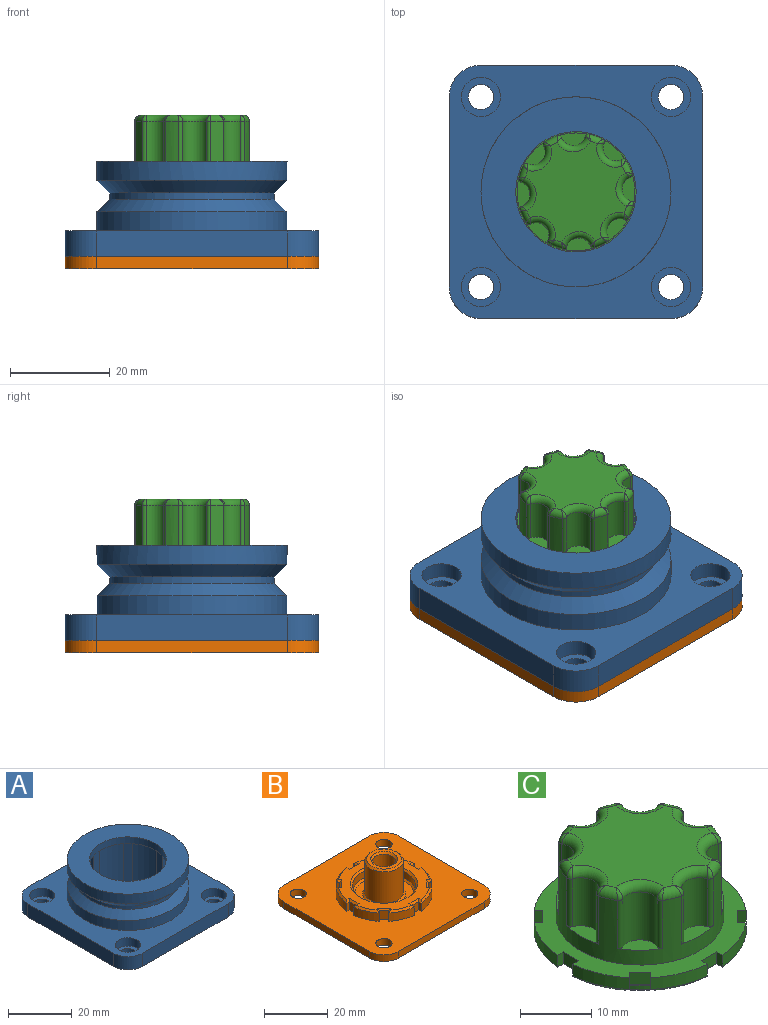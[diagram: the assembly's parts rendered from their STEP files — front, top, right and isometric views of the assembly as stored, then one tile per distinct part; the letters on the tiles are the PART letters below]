
ASSEMBLY  parts=3 mates=5
PART A: 62 faces, bbox 50.8x50.8x19.1 mm
  f0: cylinder r=19.05mm len=38.1mm, axis (0,0,-1), area 456mm2, adj f15,f61
  f1: cylinder r=3.94mm len=7.87mm, axis (0,0,-1), area 78.5mm2, adj f26,f58
  f2: cylinder r=3.94mm len=7.87mm, axis (0,0,-1), area 78.5mm2, adj f26,f56
  f3: cylinder r=3.94mm len=7.87mm, axis (0,0,-1), area 78.5mm2, adj f26,f54
  f4: cylinder r=3.94mm len=7.87mm, axis (0,0,-1), area 78.5mm2, adj f26,f52
  f5: cylinder r=15.24mm len=16.51mm, axis (0,0,-1), area 155.6mm2, adj f12,f16,f46,f50
  f6: cylinder r=15.24mm len=16.51mm, axis (0,0,-1), area 155.6mm2, adj f12,f16,f28,f47
  f7: cylinder r=15.24mm len=16.51mm, axis (0,0,-1), area 155.6mm2, adj f12,f16,f40,f44
  f8: cylinder r=15.24mm len=16.51mm, axis (0,0,-1), area 155.6mm2, adj f12,f16,f37,f41
  f9: cylinder r=15.24mm len=16.51mm, axis (0,0,-1), area 155.6mm2, adj f12,f16,f34,f38
  f10: cylinder r=15.24mm len=16.51mm, axis (0,0,-1), area 155.6mm2, adj f12,f16,f31,f35
  f11: cylinder r=15.24mm len=16.51mm, axis (0,0,-1), area 155.6mm2, adj f12,f16,f32,f49
  f12: plane 30.37x30.37mm, normal (0,0,-1), area 246.9mm2, adj f5,f6,f7,f8,f9,f10,f11,f13
  f13: cylinder r=15.24mm len=16.51mm, axis (0,0,-1), area 155.6mm2, adj f12,f16,f29,f43
  f14: cylinder r=19.05mm len=38.1mm, axis (0,0,-1), area 456mm2, adj f26,f59
  f15: plane 38.1x38.1mm, normal (0,0,1), area 682.8mm2, adj f0,f17
  f16: plane 50.8x50.8mm, normal (0,0,-1), area 1760.7mm2, adj f5,f6,f7,f8,f9,f10,f11,f13
  f17: cylinder r=12.06mm len=24.13mm, axis (0,0,1), area 192.5mm2, adj f12,f15
  f18: cylinder r=6.35mm len=6.35mm, axis (0,0,-1), area 50.7mm2, adj f16,f19,f25,f26
  f19: plane 38.1x5.08mm, normal (0,-1,0), area 193.5mm2, adj f16,f18,f20,f26
  f20: cylinder r=6.35mm len=6.35mm, axis (0,0,-1), area 50.7mm2, adj f16,f19,f21,f26
  f21: plane 38.1x5.08mm, normal (-1,0,0), area 193.5mm2, adj f16,f20,f22,f26
  f22: cylinder r=6.35mm len=6.35mm, axis (0,0,-1), area 50.7mm2, adj f16,f21,f23,f26
  f23: plane 38.1x5.08mm, normal (0,1,0), area 193.5mm2, adj f16,f22,f24,f26
  f24: cylinder r=6.35mm len=6.35mm, axis (0,0,-1), area 50.7mm2, adj f16,f23,f25,f26
  f25: plane 38.1x5.08mm, normal (1,0,0), area 193.5mm2, adj f16,f18,f24,f26
  f26: plane 50.8x50.8mm, normal (0,0,1), area 1211.2mm2, adj f1,f2,f3,f4,f14,f18,f19,f20
  f27: plane 16.51x2.54mm, normal (0,1,0), area 41.9mm2, adj f12,f16,f28,f29
  f28: plane 16.51x1.22mm, normal (1,0,0), area 20.1mm2, adj f6,f12,f16,f27
  f29: plane 16.51x1.22mm, normal (-1,0,0), area 20.1mm2, adj f12,f13,f16,f27
  f30: plane 16.51x1.8mm, normal (-0.71,-0.71,0), area 41.9mm2, adj f12,f16,f31,f32
  f31: plane 16.51x0.86mm, normal (-0.71,0.71,0), area 20.1mm2, adj f10,f12,f16,f30
  f32: plane 16.51x0.86mm, normal (0.71,-0.71,0), area 20.1mm2, adj f11,f12,f16,f30
  f33: plane 16.51x2.54mm, normal (0,-1,0), area 41.9mm2, adj f12,f16,f34,f35
  f34: plane 16.51x1.22mm, normal (-1,0,0), area 20.1mm2, adj f9,f12,f16,f33
  f35: plane 16.51x1.22mm, normal (1,0,0), area 20.1mm2, adj f10,f12,f16,f33
  f36: plane 16.51x1.8mm, normal (0.71,-0.71,0), area 41.9mm2, adj f12,f16,f37,f38
  f37: plane 16.51x0.86mm, normal (-0.71,-0.71,0), area 20.1mm2, adj f8,f12,f16,f36
  f38: plane 16.51x0.86mm, normal (0.71,0.71,0), area 20.1mm2, adj f9,f12,f16,f36
  f39: plane 16.51x2.54mm, normal (1,0,0), area 41.9mm2, adj f12,f16,f40,f41
  f40: plane 16.51x1.22mm, normal (0,-1,0), area 20.1mm2, adj f7,f12,f16,f39
  f41: plane 16.51x1.22mm, normal (0,1,0), area 20.1mm2, adj f8,f12,f16,f39
  f42: plane 16.51x1.8mm, normal (0.71,0.71,0), area 41.9mm2, adj f12,f16,f43,f44
  f43: plane 16.51x0.86mm, normal (0.71,-0.71,0), area 20.1mm2, adj f12,f13,f16,f42
  f44: plane 16.51x0.86mm, normal (-0.71,0.71,0), area 20.1mm2, adj f7,f12,f16,f42
  f45: plane 16.51x1.8mm, normal (-0.71,0.71,0), area 41.9mm2, adj f12,f16,f46,f47
  f46: plane 16.51x0.86mm, normal (0.71,0.71,0), area 20.1mm2, adj f5,f12,f16,f45
  f47: plane 16.51x0.86mm, normal (-0.71,-0.71,0), area 20.1mm2, adj f6,f12,f16,f45
  f48: plane 16.51x2.54mm, normal (-1,0,0), area 41.9mm2, adj f12,f16,f49,f50
  f49: plane 16.51x1.22mm, normal (0,1,0), area 20.1mm2, adj f11,f12,f16,f48
  f50: plane 16.51x1.22mm, normal (0,-1,0), area 20.1mm2, adj f5,f12,f16,f48
  f51: cylinder r=2.54mm len=5.08mm, axis (0,0,-1), area 30.4mm2, adj f16,f52
  f52: plane 7.87x7.87mm, normal (0,0,1), area 28.4mm2, adj f4,f51
  f53: cylinder r=2.54mm len=5.08mm, axis (0,0,-1), area 30.4mm2, adj f16,f54
  f54: plane 7.87x7.87mm, normal (0,0,1), area 28.4mm2, adj f3,f53
  f55: cylinder r=2.54mm len=5.08mm, axis (0,0,-1), area 30.4mm2, adj f16,f56
  f56: plane 7.87x7.87mm, normal (0,0,1), area 28.4mm2, adj f2,f55
  f57: cylinder r=2.54mm len=5.08mm, axis (0,0,-1), area 30.4mm2, adj f16,f58
  f58: plane 7.87x7.87mm, normal (0,0,1), area 28.4mm2, adj f1,f57
  f59: cone r=16.51mm half-angle=45deg, axis (0,0,-1), area 401.3mm2, adj f14,f60
  f60: cylinder r=16.51mm len=33.02mm, axis (0,0,-1), area 131.7mm2, adj f59,f61
  f61: cone r=16.51mm half-angle=45deg, axis (0,0,1), area 401.3mm2, adj f0,f60
PART B: 90 faces, bbox 50.8x50.8x15.9 mm
  f0: plane 50.8x50.8mm, normal (0,0,1), area 1777.7mm2, adj f1,f2,f3,f4,f5,f6,f7,f8
  f1: cylinder r=6.35mm len=6.35mm, axis (0,0,-1), area 25.3mm2, adj f0,f2,f11,f13
  f2: plane 38.1x2.54mm, normal (0,1,0), area 96.8mm2, adj f0,f1,f3,f13
  f3: cylinder r=6.35mm len=6.35mm, axis (0,0,-1), area 25.3mm2, adj f0,f2,f4,f13
  f4: plane 38.1x2.54mm, normal (-1,0,0), area 96.8mm2, adj f0,f3,f5,f13
  f5: cylinder r=6.35mm len=6.35mm, axis (0,0,-1), area 25.3mm2, adj f0,f4,f6,f13
  f6: plane 38.1x2.54mm, normal (0,-1,0), area 96.8mm2, adj f0,f5,f7,f13
  f7: cylinder r=6.35mm len=6.35mm, axis (0,0,-1), area 25.3mm2, adj f0,f6,f11,f13
  f8: cylinder r=2.54mm len=5.08mm, axis (0,0,-1), area 40.5mm2, adj f0,f13
  f9: cylinder r=2.54mm len=5.08mm, axis (0,0,-1), area 40.5mm2, adj f0,f13
  f10: cylinder r=2.54mm len=5.08mm, axis (0,0,-1), area 40.5mm2, adj f0,f13
  f11: plane 38.1x2.54mm, normal (1,0,0), area 96.8mm2, adj f0,f1,f7,f13
  f12: cylinder r=2.54mm len=5.08mm, axis (0,0,-1), area 40.5mm2, adj f0,f13
  f13: plane 50.8x50.8mm, normal (0,0,-1), area 2465mm2, adj f1,f2,f3,f4,f5,f6,f7,f8
  f14: plane 3.18x1.19mm, normal (-1,0,0), area 3.8mm2, adj f0,f15,f45,f84
  f15: plane 3.18x3.05mm, normal (0,1,0), area 9.7mm2, adj f0,f14,f16,f82
  f16: plane 3.18x1.19mm, normal (1,0,0), area 3.8mm2, adj f0,f15,f17,f80
  f17: cylinder r=15.11mm len=8.03mm, axis (0,0,-1), area 28mm2, adj f0,f16,f18,f78
  f18: plane 3.18x0.84mm, normal (-0.71,-0.71,0), area 3.8mm2, adj f0,f17,f19,f76
  f19: plane 3.18x2.16mm, normal (-0.71,0.71,0), area 9.7mm2, adj f0,f18,f20,f74
  f20: plane 3.18x0.84mm, normal (0.71,0.71,0), area 3.8mm2, adj f0,f19,f21,f72
  f21: cylinder r=15.11mm len=8.03mm, axis (0,0,-1), area 28mm2, adj f0,f20,f22,f70
  f22: plane 3.18x1.19mm, normal (0,-1,0), area 3.8mm2, adj f0,f21,f23,f68
  f23: plane 3.18x3.05mm, normal (-1,0,0), area 9.7mm2, adj f0,f22,f24,f66
  f24: plane 3.18x1.19mm, normal (0,1,0), area 3.8mm2, adj f0,f23,f25,f64
  f25: cylinder r=15.11mm len=8.03mm, axis (0,0,-1), area 28mm2, adj f0,f24,f26,f62
  f26: plane 3.18x0.84mm, normal (0.71,-0.71,0), area 3.8mm2, adj f0,f25,f27,f60
  f27: plane 3.18x2.16mm, normal (-0.71,-0.71,0), area 9.7mm2, adj f0,f26,f28,f58
  f28: plane 3.18x0.84mm, normal (-0.71,0.71,0), area 3.8mm2, adj f0,f27,f29,f59
  f29: cylinder r=15.11mm len=8.03mm, axis (0,0,-1), area 28mm2, adj f0,f28,f30,f61
  f30: plane 3.18x1.19mm, normal (1,0,0), area 3.8mm2, adj f0,f29,f31,f63
  f31: plane 3.18x3.05mm, normal (0,-1,0), area 9.7mm2, adj f0,f30,f32,f65
  f32: plane 3.18x1.19mm, normal (-1,0,0), area 3.8mm2, adj f0,f31,f33,f67
  f33: cylinder r=15.11mm len=8.03mm, axis (0,0,-1), area 28mm2, adj f0,f32,f34,f69
  f34: plane 3.18x0.84mm, normal (0.71,0.71,0), area 3.8mm2, adj f0,f33,f35,f71
  f35: plane 3.18x2.16mm, normal (0.71,-0.71,0), area 9.7mm2, adj f0,f34,f36,f73
  f36: plane 3.18x0.84mm, normal (-0.71,-0.71,0), area 3.8mm2, adj f0,f35,f37,f75
  f37: cylinder r=15.11mm len=8.03mm, axis (0,0,-1), area 28mm2, adj f0,f36,f38,f77
  f38: plane 3.18x1.19mm, normal (0,1,0), area 3.8mm2, adj f0,f37,f39,f79
  f39: plane 3.18x3.05mm, normal (1,0,0), area 9.7mm2, adj f0,f38,f40,f81
  f40: plane 3.18x1.19mm, normal (0,-1,0), area 3.8mm2, adj f0,f39,f41,f83
  f41: cylinder r=15.11mm len=8.03mm, axis (0,0,-1), area 28mm2, adj f0,f40,f42,f85
  f42: plane 3.18x0.84mm, normal (-0.71,0.71,0), area 3.8mm2, adj f0,f41,f43,f87
  f43: plane 3.18x2.16mm, normal (0.71,0.71,0), area 9.7mm2, adj f0,f42,f44,f89
  f44: plane 3.18x0.84mm, normal (0.71,-0.71,0), area 3.8mm2, adj f0,f43,f45,f88
  f45: cylinder r=15.11mm len=8.03mm, axis (0,0,-1), area 28mm2, adj f0,f14,f44,f86
  f46: cylinder r=9.91mm len=19.81mm, axis (0,0,-1), area 158.1mm2, adj f54,f57
  f47: plane 28.63x28.63mm, normal (0,0,1), area 267.4mm2, adj f57,f58,f59,f60,f61,f62,f63,f64
  f48: plane 18.54x18.54mm, normal (0,0,1), area 127.7mm2, adj f53,f54
  f49: cylinder r=3.56mm len=7.11mm, axis (0,0,-1), area 156.1mm2, adj f52,f55
  f50: cylinder r=6.1mm len=12.19mm, axis (0,0,-1), area 462.1mm2, adj f53,f56
  f51: plane 10.92x10.92mm, normal (0,0,1), area 38.5mm2, adj f55,f56
  f52: plane 7.11x7.11mm, normal (0,0,1), area 39.7mm2, adj f49
  f53: cone r=6.1mm half-angle=45deg, axis (0,0,-1), area 36.2mm2, adj f48,f50
  f54: cone r=9.91mm half-angle=45deg, axis (0,0,1), area 54.1mm2, adj f46,f48
  f55: cone r=3.56mm half-angle=45deg, axis (0,0,1), area 21.9mm2, adj f49,f51
  f56: cone r=5.46mm half-angle=45deg, axis (0,0,-1), area 32.6mm2, adj f50,f51
  f57: cone r=9.91mm half-angle=45deg, axis (0,0,1), area 57.7mm2, adj f46,f47
  f58: plane 3.05x3.05mm, normal (-0.5,-0.5,0.71), area 3.3mm2, adj f27,f47,f59,f60
  f59: plane 1.76x0.86mm, normal (-0.5,0.5,0.71), area 1mm2, adj f28,f47,f58,f61
  f60: plane 1.76x0.86mm, normal (0.5,-0.5,0.71), area 1mm2, adj f26,f47,f58,f62
  f61: cone r=14.48mm half-angle=45deg, axis (0,0,-1), area 7.1mm2, adj f29,f47,f59,f63
  f62: cone r=14.48mm half-angle=45deg, axis (0,0,-1), area 7.1mm2, adj f25,f47,f60,f64
  f63: plane 1.84x0.65mm, normal (0.71,0,0.71), area 1mm2, adj f30,f47,f61,f65
  f64: plane 1.84x0.65mm, normal (0,0.71,0.71), area 1mm2, adj f24,f47,f62,f66
  f65: plane 4.32x0.64mm, normal (0,-0.71,0.71), area 3.3mm2, adj f31,f47,f63,f67
  f66: plane 4.32x0.64mm, normal (-0.71,0,0.71), area 3.3mm2, adj f23,f47,f64,f68
  f67: plane 1.84x0.65mm, normal (-0.71,0,0.71), area 1mm2, adj f32,f47,f65,f69
  f68: plane 1.84x0.65mm, normal (0,-0.71,0.71), area 1mm2, adj f22,f47,f66,f70
  f69: cone r=14.48mm half-angle=45deg, axis (0,0,-1), area 7.1mm2, adj f33,f47,f67,f71
  f70: cone r=14.48mm half-angle=45deg, axis (0,0,-1), area 7.1mm2, adj f21,f47,f68,f72
  f71: plane 1.76x0.86mm, normal (0.5,0.5,0.71), area 1mm2, adj f34,f47,f69,f73
  f72: plane 1.76x0.86mm, normal (0.5,0.5,0.71), area 1mm2, adj f20,f47,f70,f74
  f73: plane 3.05x3.05mm, normal (0.5,-0.5,0.71), area 3.3mm2, adj f35,f47,f71,f75
  f74: plane 3.05x3.05mm, normal (-0.5,0.5,0.71), area 3.3mm2, adj f19,f47,f72,f76
  f75: plane 1.76x0.86mm, normal (-0.5,-0.5,0.71), area 1mm2, adj f36,f47,f73,f77
  f76: plane 1.76x0.86mm, normal (-0.5,-0.5,0.71), area 1mm2, adj f18,f47,f74,f78
  f77: cone r=14.48mm half-angle=45deg, axis (0,0,-1), area 7.1mm2, adj f37,f47,f75,f79
  f78: cone r=14.48mm half-angle=45deg, axis (0,0,-1), area 7.1mm2, adj f17,f47,f76,f80
  f79: plane 1.84x0.65mm, normal (0,0.71,0.71), area 1mm2, adj f38,f47,f77,f81
  f80: plane 1.84x0.65mm, normal (0.71,0,0.71), area 1mm2, adj f16,f47,f78,f82
  f81: plane 4.32x0.64mm, normal (0.71,0,0.71), area 3.3mm2, adj f39,f47,f79,f83
  f82: plane 4.32x0.64mm, normal (0,0.71,0.71), area 3.3mm2, adj f15,f47,f80,f84
  f83: plane 1.84x0.65mm, normal (0,-0.71,0.71), area 1mm2, adj f40,f47,f81,f85
  f84: plane 1.84x0.65mm, normal (-0.71,0,0.71), area 1mm2, adj f14,f47,f82,f86
  f85: cone r=14.48mm half-angle=45deg, axis (0,0,-1), area 7.1mm2, adj f41,f47,f83,f87
  f86: cone r=14.48mm half-angle=45deg, axis (0,0,-1), area 7.1mm2, adj f45,f47,f84,f88
  f87: plane 1.76x0.86mm, normal (-0.5,0.5,0.71), area 1mm2, adj f42,f47,f85,f89
  f88: plane 1.76x0.86mm, normal (0.5,-0.5,0.71), area 1mm2, adj f44,f47,f86,f89
  f89: plane 3.05x3.05mm, normal (0.5,0.5,0.71), area 3.3mm2, adj f43,f47,f87,f88
PART C: 142 faces, bbox 29.8x29.8x18.4 mm
  f0: cylinder r=6.35mm len=12.7mm, axis (0,0,-1), area 491.5mm2, adj f106,f107
  f1: cylinder r=11.81mm len=23.62mm, axis (0,0,-1), area 377.4mm2, adj f11,f37,f38,f40,f41,f42,f44,f45
  f2: plane 19.99x19.99mm, normal (0,0,1), area 253.4mm2, adj f74,f77,f78,f81,f82,f85,f86,f89
  f3: cylinder r=14.99mm len=7.94mm, axis (0,0,-1), area 17.7mm2, adj f11,f24,f35,f125
  f4: cylinder r=14.99mm len=7.94mm, axis (0,0,-1), area 17.7mm2, adj f11,f21,f31,f126
  f5: cylinder r=14.99mm len=7.94mm, axis (0,0,-1), area 17.7mm2, adj f11,f28,f33,f118
  f6: cylinder r=14.99mm len=7.94mm, axis (0,0,-1), area 17.7mm2, adj f11,f25,f30,f110
  f7: cylinder r=14.99mm len=7.94mm, axis (0,0,-1), area 17.7mm2, adj f11,f22,f27,f117
  f8: cylinder r=14.99mm len=7.94mm, axis (0,0,-1), area 17.7mm2, adj f11,f18,f19,f134
  f9: cylinder r=14.99mm len=7.94mm, axis (0,0,-1), area 17.7mm2, adj f11,f15,f16,f141
  f10: cylinder r=14.99mm len=7.94mm, axis (0,0,-1), area 17.7mm2, adj f11,f13,f36,f133
  f11: plane 29.82x29.82mm, normal (0,0,1), area 237mm2, adj f1,f3,f4,f5,f6,f7,f8,f9
  f12: plane 28.67x28.67mm, normal (0,0,-1), area 302.5mm2, adj f109,f110,f111,f112,f113,f114,f115,f116
  f13: plane 2.03x0.84mm, normal (0.71,0.71,0), area 2.4mm2, adj f10,f11,f14,f135
  f14: plane 2.16x2.16mm, normal (0.71,-0.71,0), area 6.2mm2, adj f11,f13,f15,f137
  f15: plane 2.03x0.84mm, normal (-0.71,-0.71,0), area 2.4mm2, adj f9,f11,f14,f139
  f16: plane 2.03x1.19mm, normal (0,1,0), area 2.4mm2, adj f9,f11,f17,f140
  f17: plane 3.05x2.03mm, normal (1,0,0), area 6.2mm2, adj f11,f16,f18,f138
  f18: plane 2.03x1.19mm, normal (0,-1,0), area 2.4mm2, adj f8,f11,f17,f136
  f19: plane 2.03x0.84mm, normal (-0.71,0.71,0), area 2.4mm2, adj f8,f11,f20,f132
  f20: plane 2.16x2.16mm, normal (0.71,0.71,0), area 6.2mm2, adj f11,f19,f21,f130
  f21: plane 2.03x0.84mm, normal (0.71,-0.71,0), area 2.4mm2, adj f4,f11,f20,f128
  f22: plane 2.03x0.84mm, normal (0.71,-0.71,0), area 2.4mm2, adj f7,f11,f23,f119
  f23: plane 2.16x2.16mm, normal (-0.71,-0.71,0), area 6.2mm2, adj f11,f22,f24,f121
  f24: plane 2.03x0.84mm, normal (-0.71,0.71,0), area 2.4mm2, adj f3,f11,f23,f123
  f25: plane 2.03x1.19mm, normal (0,-1,0), area 2.4mm2, adj f6,f11,f26,f111
  f26: plane 3.05x2.03mm, normal (-1,0,0), area 6.2mm2, adj f11,f25,f27,f113
  f27: plane 2.03x1.19mm, normal (0,1,0), area 2.4mm2, adj f7,f11,f26,f115
  f28: plane 2.03x0.84mm, normal (-0.71,-0.71,0), area 2.4mm2, adj f5,f11,f29,f116
  f29: plane 2.16x2.16mm, normal (-0.71,0.71,0), area 6.2mm2, adj f11,f28,f30,f114
  f30: plane 2.03x0.84mm, normal (0.71,0.71,0), area 2.4mm2, adj f6,f11,f29,f112
  f31: plane 2.03x1.19mm, normal (-1,0,0), area 2.4mm2, adj f4,f11,f32,f124
  f32: plane 3.05x2.03mm, normal (0,1,0), area 6.2mm2, adj f11,f31,f33,f122
  f33: plane 2.03x1.19mm, normal (1,0,0), area 2.4mm2, adj f5,f11,f32,f120
  f34: plane 3.05x2.03mm, normal (0,-1,0), area 6.2mm2, adj f11,f35,f36,f129
  f35: plane 2.03x1.19mm, normal (1,0,0), area 2.4mm2, adj f3,f11,f34,f127
  f36: plane 2.03x1.19mm, normal (-1,0,0), area 2.4mm2, adj f10,f11,f34,f131
  f37: plane 6.34x2.54mm, normal (0,0,1), area 9.8mm2, adj f1,f38,f39,f40
  f38: cylinder r=0.64mm len=8.26mm, axis (0,0,1), area 7.9mm2, adj f1,f37,f39,f75
  f39: cylinder r=2.54mm len=8.26mm, axis (0,0,1), area 51.8mm2, adj f37,f38,f40,f77
  f40: cylinder r=0.64mm len=8.26mm, axis (0,0,1), area 7.9mm2, adj f1,f37,f39,f79
  f41: plane 4.48x4.48mm, normal (0,0,1), area 9.8mm2, adj f1,f42,f43,f44
  f42: cylinder r=0.64mm len=8.26mm, axis (0,0,1), area 7.9mm2, adj f1,f41,f43,f80
  f43: cylinder r=2.54mm len=8.26mm, axis (0,0,1), area 51.8mm2, adj f41,f42,f44,f78
  f44: cylinder r=0.64mm len=8.26mm, axis (0,0,1), area 7.9mm2, adj f1,f41,f43,f76
  f45: plane 6.34x2.54mm, normal (0,0,1), area 9.8mm2, adj f1,f46,f47,f48
  f46: cylinder r=0.64mm len=8.26mm, axis (0,0,1), area 7.9mm2, adj f1,f45,f47,f84
  f47: cylinder r=2.54mm len=8.26mm, axis (0,0,1), area 51.8mm2, adj f45,f46,f48,f86
  f48: cylinder r=0.64mm len=8.26mm, axis (0,0,1), area 7.9mm2, adj f1,f45,f47,f88
  f49: plane 4.48x4.48mm, normal (0,0,1), area 9.8mm2, adj f1,f50,f51,f52
  f50: cylinder r=0.64mm len=8.26mm, axis (0,0,1), area 7.9mm2, adj f1,f49,f51,f96
  f51: cylinder r=2.54mm len=8.26mm, axis (0,0,1), area 51.8mm2, adj f49,f50,f52,f94
  f52: cylinder r=0.64mm len=8.26mm, axis (0,0,1), area 7.9mm2, adj f1,f49,f51,f92
  f53: plane 6.34x2.54mm, normal (0,0,1), area 9.8mm2, adj f1,f54,f55,f56
  f54: cylinder r=0.64mm len=8.26mm, axis (0,0,1), area 7.9mm2, adj f1,f53,f55,f104
  f55: cylinder r=2.54mm len=8.26mm, axis (0,0,1), area 51.8mm2, adj f53,f54,f56,f102
  f56: cylinder r=0.64mm len=8.26mm, axis (0,0,1), area 7.9mm2, adj f1,f53,f55,f100
  f57: plane 4.48x4.48mm, normal (0,0,1), area 9.8mm2, adj f1,f58,f59,f60
  f58: cylinder r=0.64mm len=8.26mm, axis (0,0,1), area 7.9mm2, adj f1,f57,f59,f99
  f59: cylinder r=2.54mm len=8.26mm, axis (0,0,1), area 51.8mm2, adj f57,f58,f60,f101
  f60: cylinder r=0.64mm len=8.26mm, axis (0,0,1), area 7.9mm2, adj f1,f57,f59,f103
  f61: plane 6.34x2.54mm, normal (0,0,1), area 9.8mm2, adj f1,f62,f63,f64
  f62: cylinder r=0.64mm len=8.26mm, axis (0,0,1), area 7.9mm2, adj f1,f61,f63,f91
  f63: cylinder r=2.54mm len=8.26mm, axis (0,0,1), area 51.8mm2, adj f61,f62,f64,f93
  f64: cylinder r=0.64mm len=8.26mm, axis (0,0,1), area 7.9mm2, adj f1,f61,f63,f95
  f65: plane 4.48x4.48mm, normal (0,0,1), area 9.8mm2, adj f1,f66,f67,f68
  f66: cylinder r=0.64mm len=8.26mm, axis (0,0,1), area 7.9mm2, adj f1,f65,f67,f83
  f67: cylinder r=2.54mm len=8.26mm, axis (0,0,1), area 51.8mm2, adj f65,f66,f68,f85
  f68: cylinder r=0.64mm len=8.26mm, axis (0,0,1), area 7.9mm2, adj f1,f65,f67,f87
  f69: cylinder r=9.53mm len=19.05mm, axis (0,0,1), area 167.2mm2, adj f108,f109
  f70: plane 18.03x18.03mm, normal (0,0,-1), area 107.7mm2, adj f107,f108
  f71: plane 11.68x11.68mm, normal (0,0,-1), area 75.6mm2, adj f72,f106
  f72: cylinder r=3.17mm len=6.35mm, axis (0,0,-1), area 50.7mm2, adj f71,f73
  f73: plane 6.35x6.35mm, normal (0,0,-1), area 31.7mm2, adj f72
  f74: torus R=10.54mm, axis (0,0,1), area 4.6mm2, adj f1,f2,f75,f76
  f75: bspline ~1.6x1.54mm, area 1.2mm2, adj f38,f74,f77
  f76: bspline ~1.62x1.6mm, area 1.2mm2, adj f44,f74,f78
  f77: torus R=3.81mm, axis (0,0,1), area 14mm2, adj f2,f39,f75,f79
  f78: torus R=3.81mm, axis (0,0,1), area 14mm2, adj f2,f43,f76,f80
  f79: bspline ~1.6x1.54mm, area 1.2mm2, adj f40,f77,f81
  f80: bspline ~1.62x1.6mm, area 1.2mm2, adj f42,f78,f82
  f81: torus R=10.54mm, axis (0,0,1), area 4.6mm2, adj f1,f2,f79,f83
  f82: torus R=10.54mm, axis (0,0,1), area 4.6mm2, adj f1,f2,f80,f84
  f83: bspline ~1.62x1.6mm, area 1.2mm2, adj f66,f81,f85
  f84: bspline ~1.6x1.54mm, area 1.2mm2, adj f46,f82,f86
  f85: torus R=3.81mm, axis (0,0,1), area 14mm2, adj f2,f67,f83,f87
  f86: torus R=3.81mm, axis (0,0,1), area 14mm2, adj f2,f47,f84,f88
  f87: bspline ~1.62x1.6mm, area 1.2mm2, adj f68,f85,f89
  f88: bspline ~1.6x1.54mm, area 1.2mm2, adj f48,f86,f90
  f89: torus R=10.54mm, axis (0,0,1), area 4.6mm2, adj f1,f2,f87,f91
  f90: torus R=10.54mm, axis (0,0,1), area 4.6mm2, adj f1,f2,f88,f92
  f91: bspline ~1.6x1.54mm, area 1.2mm2, adj f62,f89,f93
  f92: bspline ~1.62x1.6mm, area 1.2mm2, adj f52,f90,f94
  f93: torus R=3.81mm, axis (0,0,1), area 14mm2, adj f2,f63,f91,f95
  f94: torus R=3.81mm, axis (0,0,1), area 14mm2, adj f2,f51,f92,f96
  f95: bspline ~1.6x1.54mm, area 1.2mm2, adj f64,f93,f97
  f96: bspline ~1.62x1.6mm, area 1.2mm2, adj f50,f94,f98
  f97: torus R=10.54mm, axis (0,0,1), area 4.6mm2, adj f1,f2,f95,f99
  f98: torus R=10.54mm, axis (0,0,1), area 4.6mm2, adj f1,f2,f96,f100
  f99: bspline ~1.62x1.6mm, area 1.2mm2, adj f58,f97,f101
  f100: bspline ~1.6x1.54mm, area 1.2mm2, adj f56,f98,f102
  f101: torus R=3.81mm, axis (0,0,1), area 14mm2, adj f2,f59,f99,f103
  f102: torus R=3.81mm, axis (0,0,1), area 14mm2, adj f2,f55,f100,f104
  f103: bspline ~1.62x1.6mm, area 1.2mm2, adj f60,f101,f105
  f104: bspline ~1.6x1.54mm, area 1.2mm2, adj f54,f102,f105
  f105: torus R=10.54mm, axis (0,0,1), area 4.6mm2, adj f1,f2,f103,f104
  f106: cone r=6.35mm half-angle=45deg, axis (0,0,-1), area 27.5mm2, adj f0,f71
  f107: cone r=6.86mm half-angle=45deg, axis (0,0,-1), area 29.8mm2, adj f0,f70
  f108: cone r=9.02mm half-angle=45deg, axis (0,0,1), area 41.8mm2, adj f69,f70
  f109: cone r=9.53mm half-angle=45deg, axis (0,0,1), area 44.1mm2, adj f12,f69
  f110: cone r=14.99mm half-angle=45deg, axis (0,0,1), area 5.7mm2, adj f6,f12,f111,f112
  f111: plane 1.71x0.52mm, normal (0,-0.71,-0.71), area 0.8mm2, adj f12,f25,f110,f113
  f112: plane 1.57x0.85mm, normal (0.5,0.5,-0.71), area 0.8mm2, adj f12,f30,f110,f114
  f113: plane 4.06x0.51mm, normal (-0.71,0,-0.71), area 2.6mm2, adj f12,f26,f111,f115
  f114: plane 2.87x2.87mm, normal (-0.5,0.5,-0.71), area 2.6mm2, adj f12,f29,f112,f116
  f115: plane 1.71x0.52mm, normal (0,0.71,-0.71), area 0.8mm2, adj f12,f27,f113,f117
  f116: plane 1.57x0.85mm, normal (-0.5,-0.5,-0.71), area 0.8mm2, adj f12,f28,f114,f118
  f117: cone r=14.99mm half-angle=45deg, axis (0,0,1), area 5.7mm2, adj f7,f12,f115,f119
  f118: cone r=14.99mm half-angle=45deg, axis (0,0,1), area 5.7mm2, adj f5,f12,f116,f120
  f119: plane 1.57x0.85mm, normal (0.5,-0.5,-0.71), area 0.8mm2, adj f12,f22,f117,f121
  f120: plane 1.71x0.52mm, normal (0.71,0,-0.71), area 0.8mm2, adj f12,f33,f118,f122
  f121: plane 2.87x2.87mm, normal (-0.5,-0.5,-0.71), area 2.6mm2, adj f12,f23,f119,f123
  f122: plane 4.06x0.51mm, normal (0,0.71,-0.71), area 2.6mm2, adj f12,f32,f120,f124
  f123: plane 1.57x0.85mm, normal (-0.5,0.5,-0.71), area 0.8mm2, adj f12,f24,f121,f125
  f124: plane 1.71x0.52mm, normal (-0.71,0,-0.71), area 0.8mm2, adj f12,f31,f122,f126
  f125: cone r=14.99mm half-angle=45deg, axis (0,0,1), area 5.7mm2, adj f3,f12,f123,f127
  f126: cone r=14.99mm half-angle=45deg, axis (0,0,1), area 5.7mm2, adj f4,f12,f124,f128
  f127: plane 1.71x0.52mm, normal (0.71,0,-0.71), area 0.8mm2, adj f12,f35,f125,f129
  f128: plane 1.57x0.85mm, normal (0.5,-0.5,-0.71), area 0.8mm2, adj f12,f21,f126,f130
  f129: plane 4.06x0.51mm, normal (0,-0.71,-0.71), area 2.6mm2, adj f12,f34,f127,f131
  f130: plane 2.87x2.87mm, normal (0.5,0.5,-0.71), area 2.6mm2, adj f12,f20,f128,f132
  f131: plane 1.71x0.52mm, normal (-0.71,0,-0.71), area 0.8mm2, adj f12,f36,f129,f133
  f132: plane 1.57x0.85mm, normal (-0.5,0.5,-0.71), area 0.8mm2, adj f12,f19,f130,f134
  f133: cone r=14.99mm half-angle=45deg, axis (0,0,1), area 5.7mm2, adj f10,f12,f131,f135
  f134: cone r=14.99mm half-angle=45deg, axis (0,0,1), area 5.7mm2, adj f8,f12,f132,f136
  f135: plane 1.57x0.85mm, normal (0.5,0.5,-0.71), area 0.8mm2, adj f12,f13,f133,f137
  f136: plane 1.71x0.52mm, normal (0,-0.71,-0.71), area 0.8mm2, adj f12,f18,f134,f138
  f137: plane 2.87x2.87mm, normal (0.5,-0.5,-0.71), area 2.6mm2, adj f12,f14,f135,f139
  f138: plane 4.06x0.51mm, normal (0.71,0,-0.71), area 2.6mm2, adj f12,f17,f136,f140
  f139: plane 1.57x0.85mm, normal (-0.5,-0.5,-0.71), area 0.8mm2, adj f12,f15,f137,f141
  f140: plane 1.71x0.52mm, normal (0,0.71,-0.71), area 0.8mm2, adj f12,f16,f138,f141
  f141: cone r=14.99mm half-angle=45deg, axis (0,0,1), area 5.7mm2, adj f9,f12,f139,f140
PLACE A t=(-0.27,-0.29,-6.55)mm fixed
PLACE B rot(axis=(0,0,-1),90deg) t=(-0.27,-0.29,-9.09)mm
PLACE C rot(axis=(0,0,-1),87.3deg) t=(-0.27,-0.29,7.18)mm
MATE cylindrical C.f0 <-> B.f49  axis (0,0,-1) through (-0.27,-0.29,10.03)mm
MATE planar B.f6 <-> A.f21  axis (-1,0,0) through (-25.67,-0.29,-7.82)mm
MATE planar A.f21 <-> B.f6  axis (-1,0,0) through (-25.67,-0.29,-4.01)mm
MATE planar B.f29 <-> A.f5  axis (0,0,1) through (-0.27,-0.29,-6.55)mm
MATE planar A.f23 <-> B.f4  axis (0,1,0) through (-0.27,25.11,-4.01)mm
